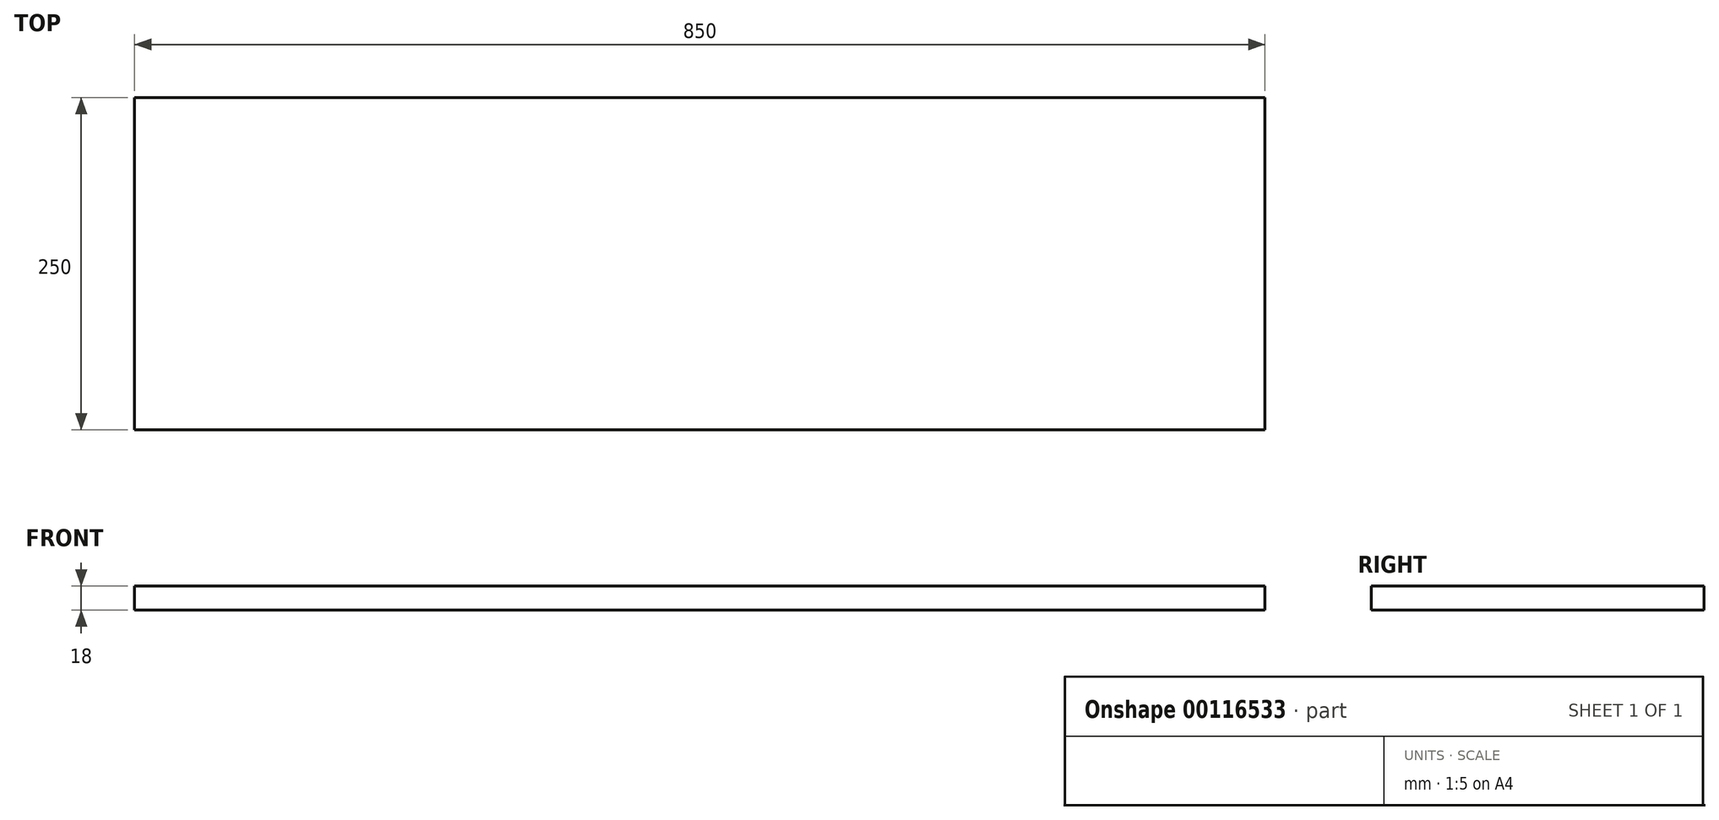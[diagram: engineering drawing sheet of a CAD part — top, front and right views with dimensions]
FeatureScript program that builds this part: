
annotation { "Feature Type Name" : "Feature", "Feature Type Description" : "" }
export const myFeature = defineFeature(function(context is Context, id is Id, definition is map)
    precondition{}
    {
        {
            var Q0;
            Q0=qCreatedBy(makeId("Top.planeOp"),FACE);
            var sketch = newSketch(context, id + "F0", { "sketchPlane" : qUnion([Q0])});
            skLineSegment(sketch, "E0.bottom", {"start": v(-57.48, 285.12) * mm, "end": v(792.52, 285.12) * mm});
            skLineSegment(sketch, "E0.top", {"start": v(-57.48, 35.12) * mm, "end": v(792.52, 35.12) * mm});
            skLineSegment(sketch, "E0.left", {"start": v(-57.48, 285.12) * mm, "end": v(-57.48, 35.12) * mm});
            skLineSegment(sketch, "E0.right", {"start": v(792.52, 285.12) * mm, "end": v(792.52, 35.12) * mm});
            skLineSegment(sketch, "E1", {"start": v(-57.48, 285.12) * mm, "end": v(62.74, 164.91) * mm});
            skLineSegment(sketch, "E2", {"start": v(62.74, 164.91) * mm, "end": v(192.52, 35.12) * mm});
            skSolve(sketch);
        }
        {
            var Q0;
            Q0=makeQuery(id+"F0.imprint","IMPRINT",FACE,{"disambiguationData":[TD([[makeQuery(id+"F0.imprint","IMPRINT",EDGE,{"derivedFrom":sQuery(id+"F0.wireOp",EDGE,"E0.bottom")}),-1.0]])]});
            var Q1;
            Q1=makeQuery(id+"F0.imprint","IMPRINT",FACE,{"disambiguationData":[TD([[makeQuery(id+"F0.imprint","IMPRINT",EDGE,{"derivedFrom":sQuery(id+"F0.wireOp",EDGE,"E0.bottom")}),-1.0]])]});
            var Q2;
            {var subQ0=sQuery(id+"F0.wireOp",EDGE,"E0.left");Q2=makeQuery(id+"F0.imprint","IMPRINT",FACE,{"disambiguationData":[TD([[makeQuery(id+"F0.imprint","IMPRINT",EDGE,{"derivedFrom":subQ0}),1.0]])]});}
            extrude(context, id + "F1", {"entities" : qUnion([Q0, Q1, Q2]), "depth" : 18 * mm});
        }
    });
